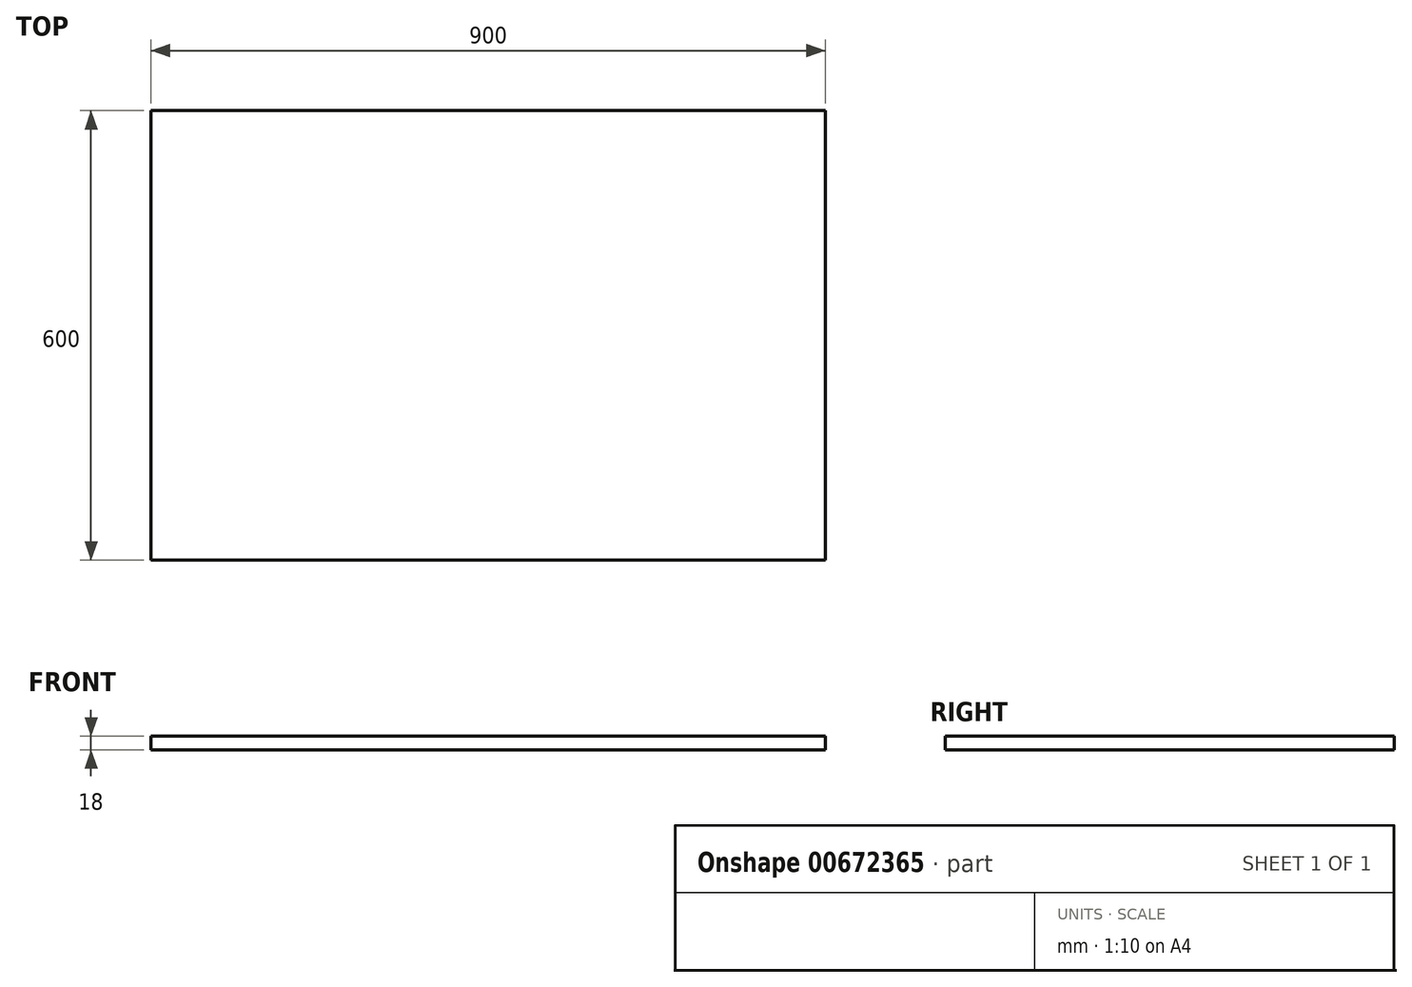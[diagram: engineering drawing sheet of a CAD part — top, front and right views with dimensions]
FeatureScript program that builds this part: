
annotation { "Feature Type Name" : "Feature", "Feature Type Description" : "" }
export const myFeature = defineFeature(function(context is Context, id is Id, definition is map)
    precondition{}
    {
        {
            var Q0;
            Q0=qCreatedBy(makeId("Top.planeOp"),FACE);
            var sketch = newSketch(context, id + "F0", { "sketchPlane" : qUnion([Q0])});
            skLineSegment(sketch, "E0.bottom", {"start": v(0, 0) * mm, "end": v(900, 0) * mm});
            skLineSegment(sketch, "E0.top", {"start": v(0, 600) * mm, "end": v(900, 600) * mm});
            skLineSegment(sketch, "E0.left", {"start": v(0, 0) * mm, "end": v(0, 600) * mm});
            skLineSegment(sketch, "E0.right", {"start": v(900, 0) * mm, "end": v(900, 600) * mm});
            skSolve(sketch);
        }
        {
            var Q0;
            Q0=makeQuery(id+"F0.imprint","IMPRINT",FACE,{"disambiguationData":[TD([[makeQuery(id+"F0.imprint","IMPRINT",EDGE,{"derivedFrom":sQuery(id+"F0.wireOp",EDGE,"E0.bottom")}),1.0]])]});
            extrude(context, id + "F1", {"entities" : qUnion([Q0]), "depth" : 18 * mm, "offsetDistance" : 25 * mm});
        }
    });
